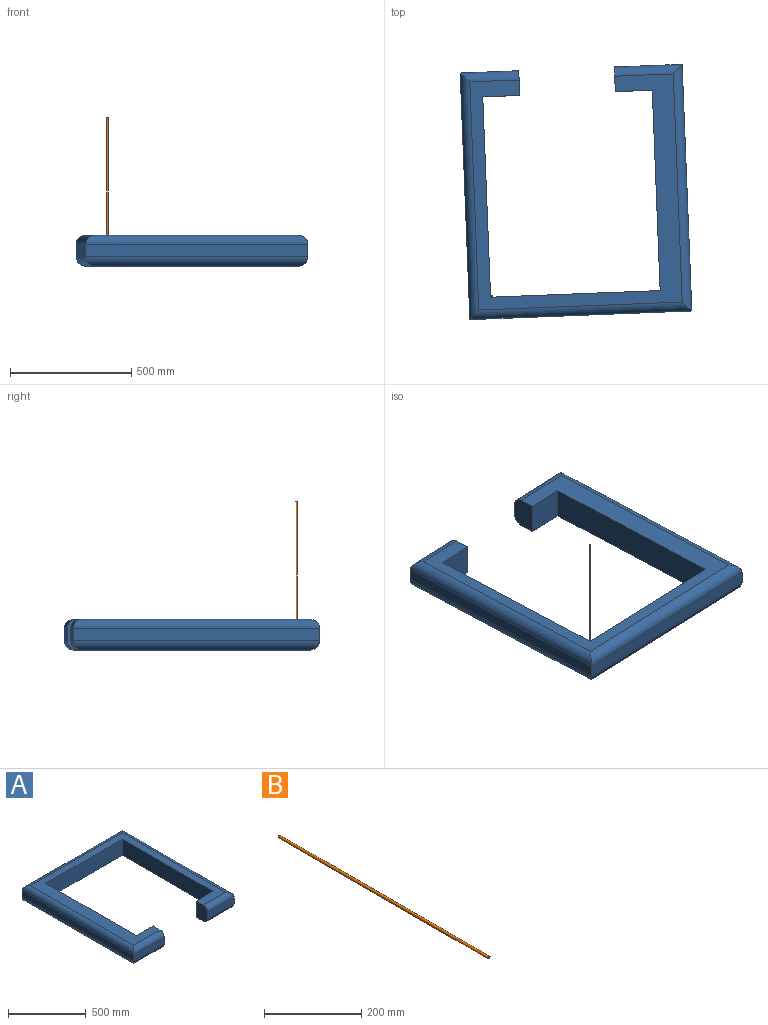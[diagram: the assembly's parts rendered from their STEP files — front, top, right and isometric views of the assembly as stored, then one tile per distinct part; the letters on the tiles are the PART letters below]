
ASSEMBLY  parts=2 mates=1
PART A: 24 faces, bbox 914.4x1016x127 mm
  f0: plane 127x101.6mm, normal (1,0,0), area 12280.2mm2, adj f1,f11,f12,f13,f17,f22
  f1: plane 152.4x127mm, normal (0,1,0), area 19354.8mm2, adj f0,f2,f12,f13
  f2: plane 825.5x127mm, normal (1,0,0), area 104838.5mm2, adj f1,f3,f12,f13
  f3: plane 698.5x127mm, normal (0,-1,0), area 88709.5mm2, adj f2,f4,f12,f13
  f4: plane 825.5x127mm, normal (-1,0,0), area 104838.5mm2, adj f3,f5,f12,f13
  f5: plane 152.4x127mm, normal (0,1,0), area 19354.8mm2, adj f4,f6,f12,f13
  f6: plane 127x101.6mm, normal (-1,0,0), area 12280.2mm2, adj f5,f7,f12,f13,f14,f19
  f7: plane 241.3x50.8mm, normal (0,-1,0), area 12258mm2, adj f6,f8,f14,f19
  f8: plane 1016x50.8mm, normal (1,0,0), area 51612.8mm2, adj f7,f9,f15,f20
  f9: plane 914.4x50.8mm, normal (0,1,0), area 46451.5mm2, adj f8,f10,f16,f21
  f10: plane 1016x50.8mm, normal (-1,0,0), area 51612.8mm2, adj f9,f11,f18,f23
  f11: plane 279.4x50.8mm, normal (0,-1,0), area 14193.5mm2, adj f0,f10,f17,f22
  f12: plane 939.8x838.2mm, normal (0,0,1), area 186128.7mm2, adj f0,f1,f2,f3,f4,f5,f6,f19
  f13: plane 939.8x838.2mm, normal (0,0,-1), area 186128.7mm2, adj f0,f1,f2,f3,f4,f5,f6,f14
  f14: cylinder r=38.1mm len=241.3mm, axis (1,0,0), area 13612.6mm2, adj f6,f7,f13,f15
  f15: cylinder r=38.1mm len=1016mm, axis (0,1,0), area 59147.8mm2, adj f8,f13,f14,f16
  f16: cylinder r=38.1mm len=914.4mm, axis (-1,0,0), area 53067.3mm2, adj f9,f13,f15,f18
  f17: cylinder r=38.1mm len=279.4mm, axis (1,0,0), area 15892.8mm2, adj f0,f11,f13,f18
  f18: cylinder r=38.1mm len=1016mm, axis (0,-1,0), area 59147.8mm2, adj f10,f13,f16,f17
  f19: cylinder r=38.1mm len=241.3mm, axis (-1,0,0), area 13612.6mm2, adj f6,f7,f12,f20
  f20: cylinder r=38.1mm len=1016mm, axis (0,-1,0), area 59147.8mm2, adj f8,f12,f19,f21
  f21: cylinder r=38.1mm len=914.4mm, axis (1,0,0), area 53067.3mm2, adj f9,f12,f20,f23
  f22: cylinder r=38.1mm len=279.4mm, axis (-1,0,0), area 15892.8mm2, adj f0,f11,f12,f23
  f23: cylinder r=38.1mm len=1016mm, axis (0,1,0), area 59147.8mm2, adj f10,f12,f21,f22
PART B: 3 faces, bbox 6.4x609.6x6.4 mm
  f0: cylinder r=3.17mm len=609.6mm, axis (0,1,0), area 12161mm2, adj f1,f2
  f1: plane 6.35x6.35mm, normal (0,-1,0), area 31.7mm2, adj f0
  f2: plane 6.35x6.35mm, normal (0,1,0), area 31.7mm2, adj f0
PLACE A rot(axis=(0,0,-1),177.8deg) t=(36.92,682.47,-62.65)mm
PLACE B rot(axis=(1,0,0),90deg) t=(-950.3,90.75,338.65)mm
MATE planar B.f0 <-> A.f13  axis (0,0,-1) through (-318.41,90.75,-62.65)mm
